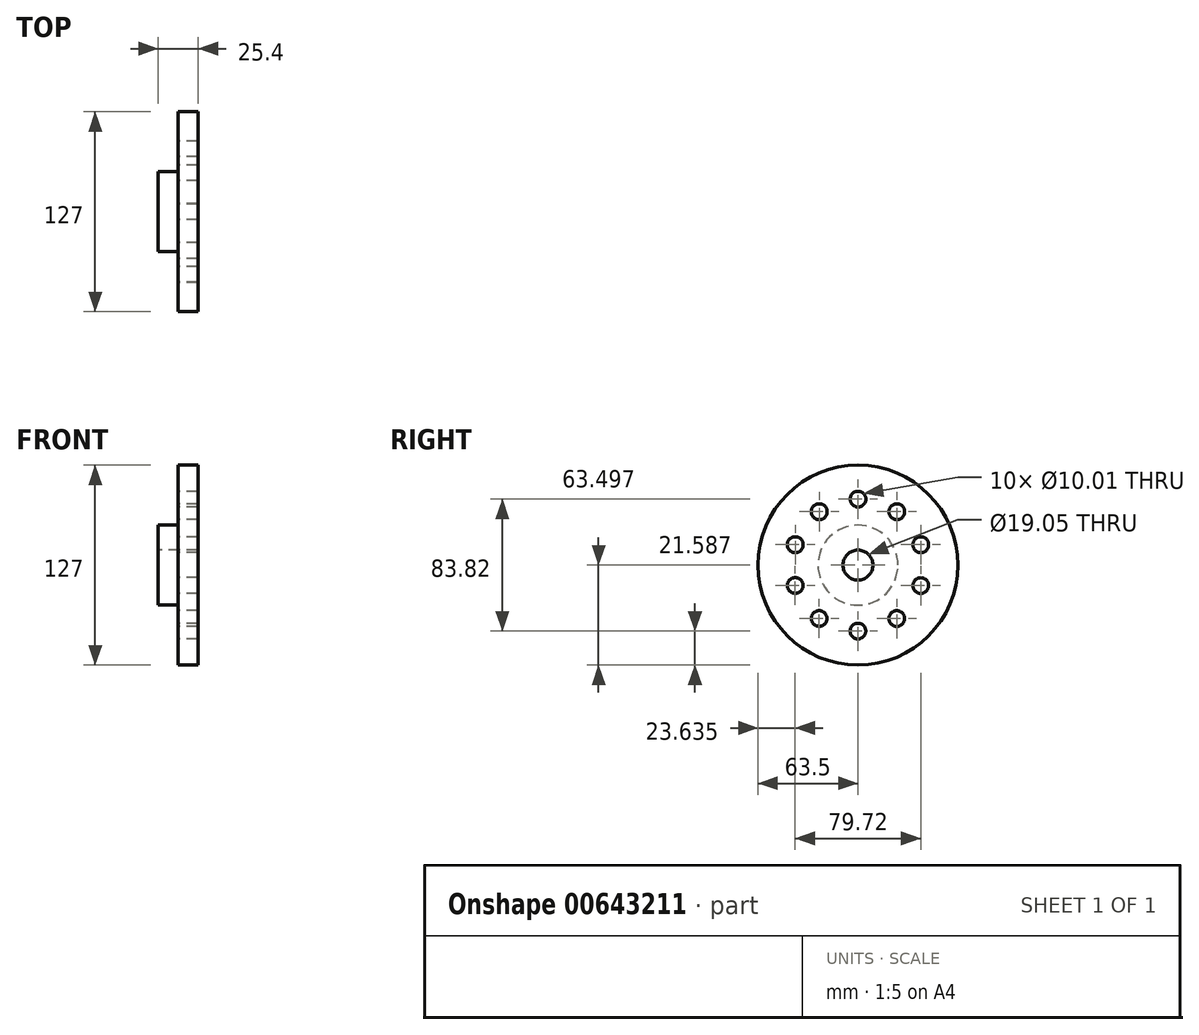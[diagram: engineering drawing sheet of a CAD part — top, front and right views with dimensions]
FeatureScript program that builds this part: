
annotation { "Feature Type Name" : "Feature", "Feature Type Description" : "" }
export const myFeature = defineFeature(function(context is Context, id is Id, definition is map)
    precondition{}
    {
        {
            var Q0;
            Q0=qCreatedBy(makeId("Front.planeOp"),FACE);
            var sketch = newSketch(context, id + "F0", { "sketchPlane" : qUnion([Q0])});
            skLineSegment(sketch, "E0", {"start": v(-25.15, 29.47) * mm, "end": v(-12.45, 29.47) * mm});
            skLineSegment(sketch, "E1", {"start": v(-12.45, 29.47) * mm, "end": v(-12.45, -24.5) * mm});
            skLineSegment(sketch, "E2", {"start": v(-12.45, -24.5) * mm, "end": v(-37.85, -24.5) * mm});
            skLineSegment(sketch, "E3", {"start": v(-37.85, -24.5) * mm, "end": v(-37.85, -8.63) * mm});
            skLineSegment(sketch, "E4", {"start": v(-37.85, -8.63) * mm, "end": v(-25.15, -8.63) * mm});
            skLineSegment(sketch, "E5", {"start": v(-25.15, -8.63) * mm, "end": v(-25.15, 29.47) * mm});
            skLineSegment(sketch, "E6", {"start": v(-74.45, -34.03) * mm, "end": v(16.18, -34.03) * mm, "construction": true});
            skSolve(sketch);
        }
        {
            var Q0;
            Q0 = qSketchRegion(id + "F0", true);
            var Q1;
            Q1=sQuery(id+"F0.wireOp",EDGE,"E6");
            revolve(context, id + "F1", {"entities" : qUnion([Q0]), "axis" : qUnion([Q1]), "revolveType" : RevolveType.FULL});
        }
        {
            var Q0;
            Q0=makeQuery(id+"F1.opRevolve","SWEPT_FACE",FACE,{"disambiguationData":[OSD([sQuery(id+"F0.wireOp",EDGE,"E5")])]});
            var sketch = newSketch(context, id + "F2", { "sketchPlane" : qUnion([Q0])});
            skCircle(sketch, "E7", {"center": v(0, -34.03) * mm, "radius": 41.91 * mm, "construction": true});
            skCircle(sketch, "E8", {"center": v(0, 7.88) * mm, "radius": 5 * mm});
            skCircle(sketch, "E9", {"center": v(24.63, -0.12) * mm, "radius": 5 * mm});
            skCircle(sketch, "E10", {"center": v(39.85, -21.07) * mm, "radius": 5 * mm});
            skCircle(sketch, "E11", {"center": v(39.87, -46.96) * mm, "radius": 5 * mm});
            skCircle(sketch, "E12", {"center": v(24.66, -67.92) * mm, "radius": 5 * mm});
            skCircle(sketch, "E13", {"center": v(-24.6, -67.96) * mm, "radius": 5 * mm});
            skCircle(sketch, "E14", {"center": v(0.03, -75.94) * mm, "radius": 5 * mm});
            skCircle(sketch, "E15", {"center": v(-39.84, -47.03) * mm, "radius": 5 * mm});
            skCircle(sketch, "E16", {"center": v(-39.85, -21.07) * mm, "radius": 5 * mm});
            skCircle(sketch, "E17", {"center": v(-24.63, -0.12) * mm, "radius": 5 * mm});
            skLineSegment(sketch, "E18", {"start": v(0, -34.03) * mm, "end": v(41.91, -34.03) * mm});
            skSolve(sketch);
        }
        {
            var Q0;
            Q0 = qSketchRegion(id + "F2", true);
            extrude(context, id + "F3", {"entities" : qUnion([Q0]), "operationType" : NewBodyOperationType.REMOVE, "oppositeDirection" : true, "depth" : 25.4 * mm, "offsetDistance" : 25.4 * mm});
        }
    });
